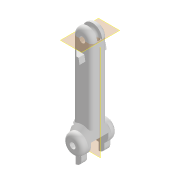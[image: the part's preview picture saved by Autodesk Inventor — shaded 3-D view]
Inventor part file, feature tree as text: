
AUTODESK INVENTOR PART (.ipt)
format: ipt  version: 2020.2 (Build 242310000, 310)  size: 321,024 bytes
history: native  units: mm
features: sketch x9, extrude x8, mirror x5, chamfer x3, fillet x3, plane x2, revolve x1
ambient origin geometry x8: Origin, YZ Plane, XZ Plane, XY Plane, X Axis, Y Axis, Z Axis, Center Point
bodies: Solid1 (feature_tree)
feature tree (31):
  extrude  "base"  Depth=45.0mm
  extrude  "joint"  Depth=10.0mm
  plane  "Work Plane1"
  mirror  "Mirror1"
  chamfer  "Chamfer1"  Distance=8.0mm
  extrude  "joint_2"  Depth=3.0mm
  fillet  "Fillet2"  Radius=5.0mm
  plane  "Work Plane2"
  revolve  "Revolution2"  [1 undecoded]
  extrude  "Extrusion8"  Depth=2.0mm TaperAngle=45.0deg
  extrude  "Extrusion9"  Depth=2.0mm
  mirror  "Mirror4"
  fillet  "Fillet4"  Radius=3.5mm
  extrude  "Extrusion10"  Depth=40.0mm TaperAngle=0.0deg
  mirror  "Mirror5"
  chamfer  "Chamfer3"  Distance=13.962634mm
  extrude  "lock_1"  Depth=2.0mm
  mirror  "Mirror2"
  chamfer  "Chamfer2"  Distance=3.0mm
  extrude  "lock_2"  Depth=3.0mm TaperAngle=45.0deg
  mirror  "Mirror3"
  fillet  "Fillet3"  Radius=4.0mm
  sketch  "Sketch1"  dims[d0=3.0mm d1=45.0mm]
  sketch  "Sketch2"  dims[d2=3.0mm d3=10.0mm]
  sketch  "Sketch4"  dims[d4=10.0mm d5=8.0mm d6=0.0mm]
  sketch  "Sketch7"  dims[d7=10.0mm d8=3.0mm d9=5.0mm d10=0.0mm]
  sketch  "Sketch8"  dims[d12=10.5mm d13=3.0mm]
  sketch  "Sketch9"  dims[d14=9.0mm d15=0.0mm d16=2.0mm d17=2.0mm d18=45.0deg]
  sketch  "Sketch10"  dims[d19=2.0mm d20=3.5mm d21=3.5mm]
  sketch  "Sketch11"  dims[d23=2.5mm d24=40.0mm d25=0.0mm]
  sketch  "Sketch12"  dims[d32=6.0mm d33=13.962634mm d34=5.0mm d35=3.0mm d36=0.0mm d37=3.0mm d38=2.0mm d39=45.0deg d40=4.0mm d41=3.0mm d42=3.0mm d43=0.0mm d44=3.0mm d45=4.0mm d46=90.0deg d47=3.5mm d48=2.5mm d49=180.0deg d50=5.0mm d51=0.0mm d52=4.0mm d53=3.0mm d54=3.0mm d55=0.0mm d56=3.0mm d57=6.0mm d58=3.0mm d59=13.962634mm d60=3.0mm d61=0.0mm d62=3.0mm d63=2.0mm d64=45.0deg]
note: 1 required parameter value undecoded (feature->parameter linkage not recoverable at this tier; creation-order binding heuristic only, values carry confidence <= 0.55)
